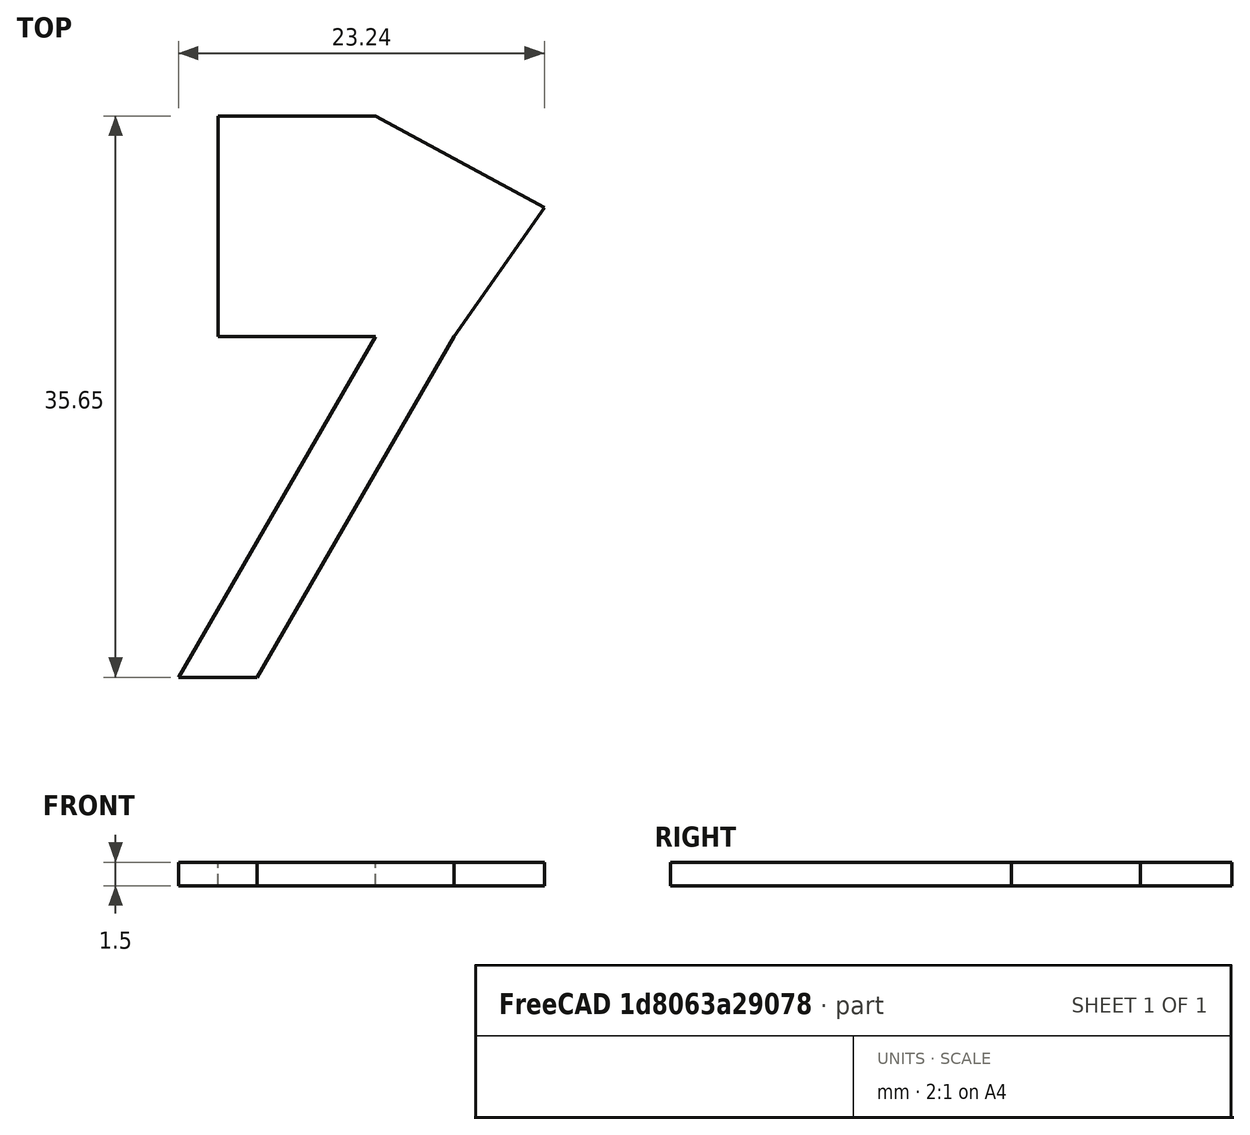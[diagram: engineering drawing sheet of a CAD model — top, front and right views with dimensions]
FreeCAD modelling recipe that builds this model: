
FCSTD DOCUMENT  (FreeCAD 0.17R13519 (Git))
Label: DingDengJia-jwei-1.0
License: All rights reserved
LicenseURL: http://en.wikipedia.org/wiki/All_rights_reserved
objects: Sketcher::SketchObject×1, PartDesign::Pad×1, PartDesign::Body×1
note: 4 computed .brp shape members not serialized (recipe doc carries the construction recipe); baked Part::Feature solids carry a one-line shape summary decoded from their .brp

FEATURE [Sketcher::SketchObject] Sketch
  MapMode = 5
  Support = -> [XY_Plane]
  sketch-geometry (8):
    g0: LineSegment StartX=0 StartY=0 StartZ=0 EndX=12.5 EndY=21.6506 EndZ=0
    g1: LineSegment StartX=0 StartY=0 StartZ=0 EndX=5 EndY=0 EndZ=0
    g2: LineSegment StartX=5 StartY=0 StartZ=0 EndX=17.5 EndY=21.6506 EndZ=0
    g3: LineSegment StartX=12.5 StartY=21.6506 StartZ=0 EndX=2.5 EndY=21.6506 EndZ=0
    g4: LineSegment StartX=17.5 StartY=21.6506 StartZ=0 EndX=23.2358 EndY=29.8422 EndZ=0
    g5: LineSegment StartX=23.2358 StartY=29.8422 StartZ=0 EndX=12.5 EndY=35.6506 EndZ=0
    g6: LineSegment StartX=2.5 StartY=21.6506 StartZ=0 EndX=2.5 EndY=35.6506 EndZ=0
    g7: LineSegment StartX=2.5 StartY=35.6506 StartZ=0 EndX=12.5 EndY=35.6506 EndZ=0
  constraints (24):
    c: Coincident(g1,g0)
    c: Horizontal(g1)
    c: Coincident(g2,g1)
    c: DistanceX(g1,g1) = 5
    c: Distance(g0) = 25
    c: Angle(g1,g0) = 1.0472
    c: PointOnObject(g0,g-2)
    c: Coincident(g3,g0)
    c: Distance(g3) = 10
    c: Coincident(g0,g-1)
    c: Coincident(g4,g2)
    c: Angle(g4,g2) = 3.22886
    c: Angle(g2,g1) = 2.0944
    c: Distance(g2) = 25
    c: Distance(g4) = 10
    c: Coincident(g5,g4)
    c: Coincident(g6,g3)
    c: Vertical(g6)
    c: DistanceY(g6,g6) = 14
    c: Horizontal(g3)
    c: Coincident(g7,g6)
    c: Horizontal(g7)
    c: DistanceX(g7,g7) = 10
    c: Coincident(g5,g7)
FEATURE [PartDesign::Pad] Pad
  Length = 1.5
  Length2 = 100
  Profile = -> Sketch
  Type = 0
FEATURE [PartDesign::Body] Body
  Group = -> [Sketch,Pad]
  Origin = -> Origin
  Tip = -> Pad
